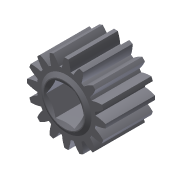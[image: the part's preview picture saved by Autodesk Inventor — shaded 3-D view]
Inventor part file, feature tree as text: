
AUTODESK INVENTOR PART (.ipt)
format: ipt  version: 2011 (Build 150239000, 239)  size: 242,176 bytes
history: native  units: mm (DEFAULTED — no unit token found)
features: sketch x5, other x4, extrude x3, plane x3, revolve x1, chamfer x1
ambient origin geometry x8: Origin, YZ Plane, XZ Plane, XY Plane, X Axis, Y Axis, Z Axis, Center Point
bodies: Solid1 (feature_tree)
feature tree (17):
  other  "Gear 16T 20dp 375hex"
  extrude  "Extrusion1"  Depth=14.4272mm TaperAngle=0.0deg
  plane  "Work Plane1"
  plane  "Work Plane2"
  plane  "Work Plane3"
  other  "Spur Gear"
  extrude  "Extrusion3"  Depth=76.2mm TaperAngle=0.0deg
  extrude  "Extrusion4"  TaperAngle=0.0deg  [1 undecoded]
  revolve  "Revolution1"  [1 undecoded]
  chamfer  "Chamfer1"  Distance=46.355mm
  sketch  "Sketch1"  dims[d0=22.86mm d1=14.4272mm d2=0.0mm]
  sketch  "Sketch2"  dims[d3=20.32mm d4=76.2mm d5=0.0mm]
  other  "Srf1"
  sketch  "Sketch6"  dims[d6=0.0mm d7=1.963495mm d9=0.0mm]
  sketch  "Sketch7"  dims[d14=0.0mm d15=46.355mm d16=0.0mm d17=0.0mm d18=0.0mm d19=46.355mm]
  sketch  "Sketch8"  dims[d23=14.605mm d24=0.635mm d25=0.0mm d26=9.525mm d27=0.635mm d28=0.0mm d29=15.0622mm d30=7.3152mm d31=4.7625mm d32=26.345745mm d33=26.345745mm d34=1.143mm d35=0.254mm d36=90.0deg d37=1.143mm d38=3.175mm d39=26.345745mm]
  other  "Pitch Diameter"
note: 2 required parameter values undecoded (feature->parameter linkage not recoverable at this tier; creation-order binding heuristic only, values carry confidence <= 0.55)